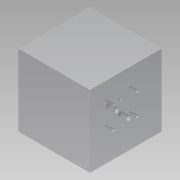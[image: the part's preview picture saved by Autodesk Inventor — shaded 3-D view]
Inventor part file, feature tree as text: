
AUTODESK INVENTOR PART (.ipt)
format: ipt  version: 2014 (Build 180170000, 170)  size: 184,832 bytes
history: native  units: mm
features: other x48, extrude x13, sketch x13
ambient origin geometry x8: Origin, YZ Plane, XZ Plane, XY Plane, X Axis, Y Axis, Z Axis, Center Point
bodies: 实体1 (feature_tree)
feature tree (74):
  extrude  "拉伸1"  Depth=101.0mm
  other  "UCS1"
  other  "UCS2"
  other  "UCS3"
  other  "UCS4"
  other  "UCS5"
  other  "UCS6"
  extrude  "拉伸2"  Depth=125.0mm
  extrude  "拉伸3"  Depth=6.8mm
  extrude  "拉伸4"  Depth=41.3mm
  extrude  "拉伸5"  TaperAngle=0.0deg  [1 undecoded]
  extrude  "拉伸6"  Depth=82.6mm
  extrude  "拉伸7"  TaperAngle=0.0deg  [1 undecoded]
  extrude  "拉伸8"  Depth=4.0mm TaperAngle=0.0deg
  extrude  "拉伸9"  Depth=4.0mm
  extrude  "拉伸10"  Depth=16.0mm TaperAngle=0.0deg
  extrude  "拉伸11"  Depth=16.0mm
  extrude  "拉伸12"  Depth=16.0mm
  extrude  "拉伸13"  Depth=16.0mm
  sketch  "草图1"  dims[d0=250.0mm d1=0.0mm]
  sketch  "草图2"  dims[d2=0.0mm d3=0.0mm d4=0.0mm d5=0.0mm d6=0.0mm d7=0.0mm]
  sketch  "草图3"  dims[d8=0.0mm d9=0.0mm d10=0.0mm d11=0.0mm d12=0.0mm d13=0.0mm]
  sketch  "草图4"  dims[d14=0.0mm d15=0.0mm d16=0.0mm d17=0.0mm d18=0.0mm d19=0.0mm]
  sketch  "草图5"  dims[d20=0.0mm d21=0.0mm d22=0.0mm d23=0.0mm d24=0.0mm d25=0.0mm]
  sketch  "草图6"  dims[d26=0.0mm d27=0.0mm d28=0.0mm d29=0.0mm d30=0.0mm d31=0.0mm]
  sketch  "草图7"  dims[d32=0.0mm d33=0.0mm d34=0.0mm d35=0.0mm d36=0.0mm d37=0.0mm d38=101.0mm]
  sketch  "草图8"  dims[d39=95.0mm d40=125.0mm]
  sketch  "草图9"  dims[d41=124.0mm d44=6.8mm]
  sketch  "草图10"  dims[d45=38.1mm d46=41.3mm]
  sketch  "草图11"  dims[d47=76.2mm d48=0.0mm]
  sketch  "草图12"  dims[d49=76.2mm d50=82.6mm]
  sketch  "草图13"  dims[d51=82.6mm d52=0.0mm d53=26.0mm d54=0.0mm d55=8.0mm d56=16.0mm d57=0.0mm d58=16.0mm d59=-10.297443mm d60=16.0mm d61=-10.297443mm d62=16.0mm d63=-10.297443mm d64=16.0mm d65=-10.297443mm d66=14.7mm d67=54.0mm d68=11.1mm d69=31.0mm d70=0.0mm d71=31.0mm d72=-10.297443mm d73=14.7mm d74=52.4mm d75=9.5mm d76=30.0mm d77=0.0mm d78=30.0mm d79=-10.297443mm d80=7.5mm d81=23.8mm d82=79.4mm d83=4.0mm d84=0.0mm d85=4.0mm d86=-10.297443mm]
  other  "UCS1: YZ 平面"
  other  "UCS1: XZ 平面"
  other  "UCS1: XY 平面"
  other  "UCS1: X 轴"
  other  "UCS1: Y 轴"
  other  "UCS1: Z 轴"
  other  "UCS1: 原点"
  other  "UCS2: YZ 平面"
  other  "UCS2: XZ 平面"
  other  "UCS2: XY 平面"
  other  "UCS2: X 轴"
  other  "UCS2: Y 轴"
  other  "UCS2: Z 轴"
  other  "UCS2: 原点"
  other  "UCS3: YZ 平面"
  other  "UCS3: XZ 平面"
  other  "UCS3: XY 平面"
  other  "UCS3: X 轴"
  other  "UCS3: Y 轴"
  other  "UCS3: Z 轴"
  other  "UCS3: 原点"
  other  "UCS4: YZ 平面"
  other  "UCS4: XZ 平面"
  other  "UCS4: XY 平面"
  other  "UCS4: X 轴"
  other  "UCS4: Y 轴"
  other  "UCS4: Z 轴"
  other  "UCS4: 原点"
  other  "UCS5: YZ 平面"
  other  "UCS5: XZ 平面"
  other  "UCS5: XY 平面"
  other  "UCS5: X 轴"
  other  "UCS5: Y 轴"
  other  "UCS5: Z 轴"
  other  "UCS5: 原点"
  other  "UCS6: YZ 平面"
  other  "UCS6: XZ 平面"
  other  "UCS6: XY 平面"
  other  "UCS6: X 轴"
  other  "UCS6: Y 轴"
  other  "UCS6: Z 轴"
  other  "UCS6: 原点"
note: 2 required parameter values undecoded (feature->parameter linkage not recoverable at this tier; creation-order binding heuristic only, values carry confidence <= 0.55)
